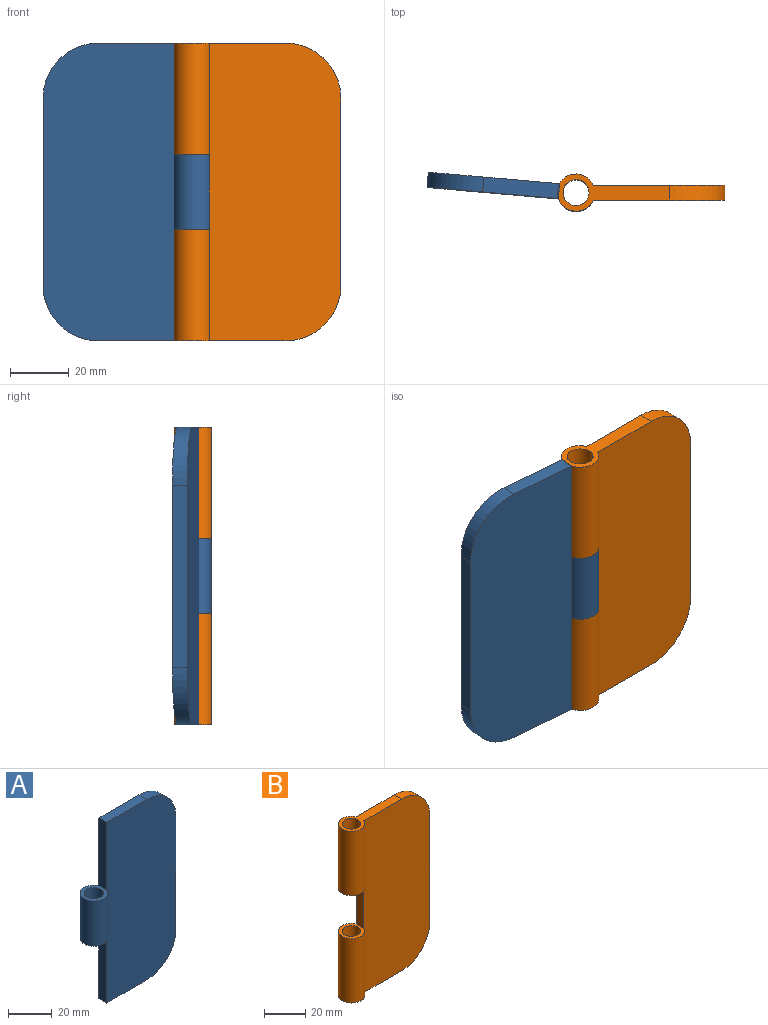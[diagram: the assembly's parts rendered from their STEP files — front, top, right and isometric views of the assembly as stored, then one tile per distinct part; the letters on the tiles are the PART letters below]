
ASSEMBLY  parts=2 mates=1
PART A: 13 faces, bbox 57.2x12.7x101.6 mm
  f0: cylinder r=6.35mm len=25.4mm, axis (0,0,1), area 880.7mm2, adj f7,f8,f9,f11
  f1: cylinder r=4.45mm len=25.4mm, axis (0,0,1), area 709.4mm2, adj f9,f11
  f2: plane 25.95x5.08mm, normal (0,0,1), area 131.8mm2, adj f5,f7,f8,f12
  f3: plane 25.12x5.08mm, normal (0,0,-1), area 127.6mm2, adj f6,f7,f8,f10
  f4: plane 62.09x5.08mm, normal (1,0,0), area 315.4mm2, adj f5,f6,f7,f8
  f5: cylinder r=19.05mm len=19.86mm, axis (0,1,0), area 156.1mm2, adj f2,f4,f7,f8
  f6: cylinder r=19.05mm len=19.86mm, axis (0,1,0), area 159.2mm2, adj f3,f4,f7,f8
  f7: plane 101.6x45mm, normal (0,-1,0), area 4414mm2, adj f0,f2,f3,f4,f5,f6,f10,f12
  f8: plane 101.6x45mm, normal (0,1,0), area 4414mm2, adj f0,f2,f3,f4,f5,f6,f10,f12
  f9: plane 12.7x12.17mm, normal (0,0,-1), area 62.8mm2, adj f0,f1,f10
  f10: plane 38.1x5.08mm, normal (-1,0,0), area 193.5mm2, adj f3,f7,f8,f9
  f11: plane 12.7x12.17mm, normal (0,0,1), area 62.8mm2, adj f0,f1,f12
  f12: plane 38.1x5.08mm, normal (-1,0,0), area 193.5mm2, adj f2,f7,f8,f11
PART B: 17 faces, bbox 57.2x12.7x101.6 mm
  f0: cylinder r=6.35mm len=38.1mm, axis (0,0,1), area 1321mm2, adj f7,f8,f9,f11,f13,f15
  f1: cylinder r=4.45mm len=38.1mm, axis (0,0,1), area 1064.1mm2, adj f5,f9,f11,f13,f15
  f2: plane 62.09x5.08mm, normal (1,0,0), area 315.4mm2, adj f3,f6,f7,f8
  f3: cylinder r=19.05mm len=19.86mm, axis (0,1,0), area 156.1mm2, adj f2,f4,f7,f8
  f4: plane 38.12x12.7mm, normal (0,0,1), area 194.6mm2, adj f3,f7,f8,f10,f12
  f5: plane 27.3x5.08mm, normal (0,0,-1), area 135.9mm2, adj f1,f6,f7,f8,f9,f11
  f6: cylinder r=19.05mm len=19.86mm, axis (0,1,0), area 159.2mm2, adj f2,f5,f7,f8
  f7: plane 101.6x45mm, normal (0,-1,0), area 4414mm2, adj f0,f2,f3,f4,f5,f6,f10,f16
  f8: plane 101.6x45mm, normal (0,1,0), area 4414mm2, adj f0,f2,f3,f4,f5,f6,f10,f16
  f9: plane 2.17x0mm, normal (0,-1,0), area 0mm2, adj f0,f1,f5,f13
  f10: cylinder r=6.35mm len=38.1mm, axis (0,0,1), area 1321mm2, adj f4,f7,f8,f14
  f11: plane 2.17x0mm, normal (0,1,0), area 0mm2, adj f0,f1,f5,f13
  f12: cylinder r=4.45mm len=38.1mm, axis (0,0,1), area 1064.1mm2, adj f4,f14
  f13: plane 12.7x12.17mm, normal (0,0,-1), area 54.5mm2, adj f0,f1,f9,f11
  f14: plane 12.7x12.17mm, normal (0,0,-1), area 62.8mm2, adj f10,f12,f16
  f15: plane 12.7x12.17mm, normal (0,0,1), area 62.8mm2, adj f0,f1,f16
  f16: plane 25.4x5.08mm, normal (-1,0,0), area 129mm2, adj f7,f8,f14,f15
PLACE A rot(axis=(0,0,1),175deg) t=(49.01,67.15,-15.31)mm
PLACE B t=(49.23,72.22,-15.31)mm
MATE revolute A.f0 <-> B.f0  axis (0,0,1) through (49.23,69.68,48.19)mm
